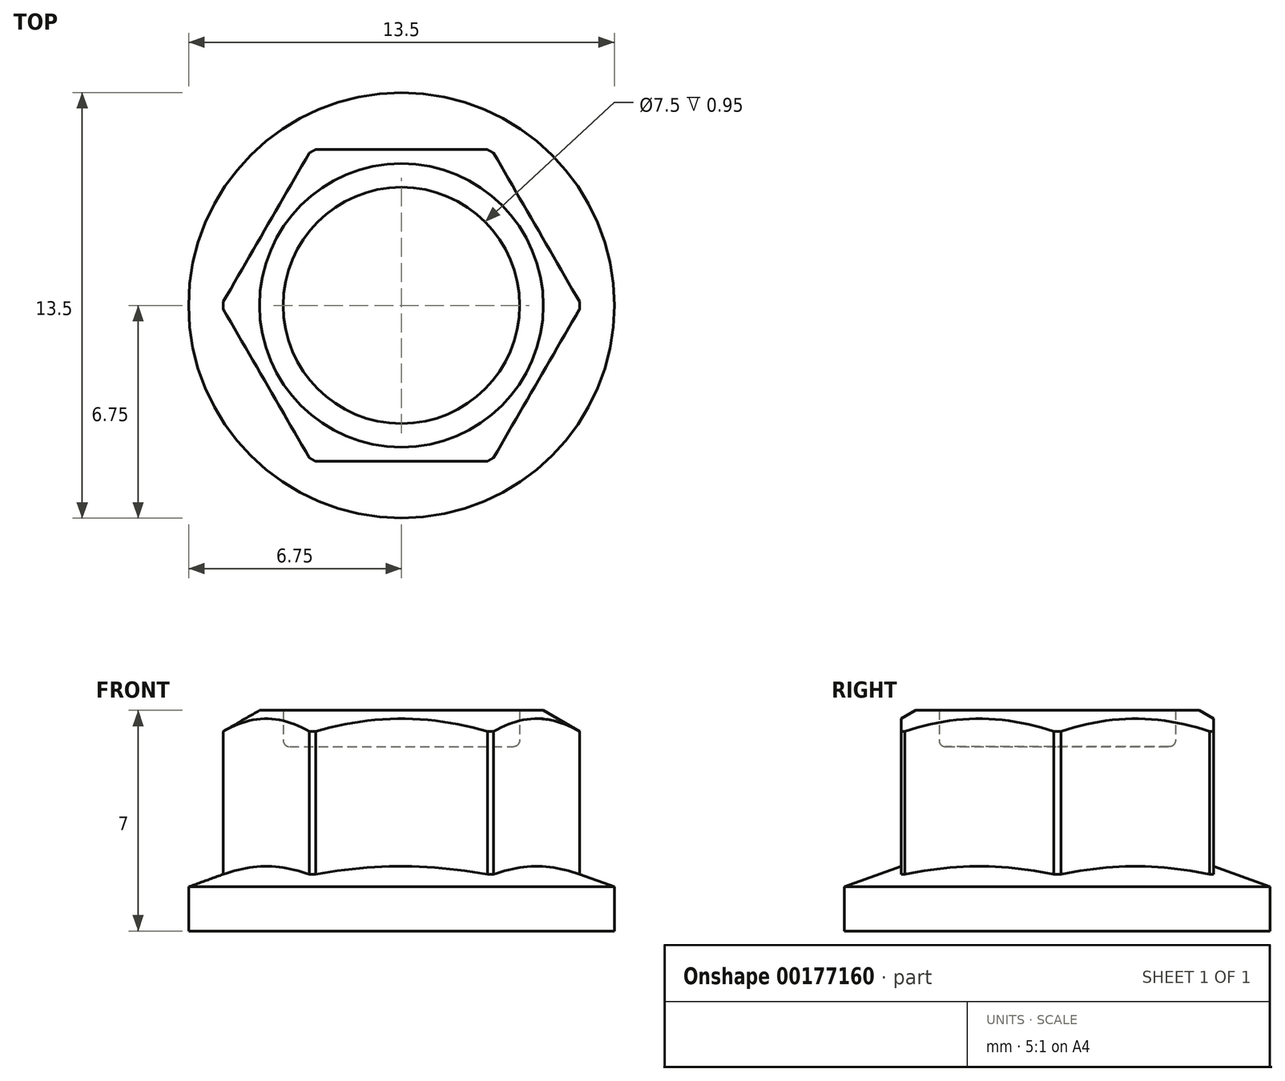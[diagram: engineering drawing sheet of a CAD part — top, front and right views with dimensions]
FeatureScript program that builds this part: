
annotation { "Feature Type Name" : "Feature", "Feature Type Description" : "" }
export const myFeature = defineFeature(function(context is Context, id is Id, definition is map)
    precondition{}
    {
        {
            var Q0;
            Q0=qCreatedBy(makeId("Front.planeOp"),FACE);
            var sketch = newSketch(context, id + "F0", { "sketchPlane" : qUnion([Q0])});
            skLineSegment(sketch, "E0", {"start": v(0, 0) * mm, "end": v(0, 5.85) * mm});
            skLineSegment(sketch, "E1", {"start": v(3.75, 7) * mm, "end": v(4.5, 7) * mm});
            skLineSegment(sketch, "E2", {"start": v(5.65, 6.34) * mm, "end": v(5.65, 1.8) * mm});
            skLineSegment(sketch, "E3", {"start": v(5.65, 1.8) * mm, "end": v(6.75, 1.4) * mm});
            skLineSegment(sketch, "E4", {"start": v(6.75, 1.4) * mm, "end": v(6.75, 0) * mm});
            skLineSegment(sketch, "E5", {"start": v(6.75, 0) * mm, "end": v(0, 0) * mm});
            skLineSegment(sketch, "E6", {"start": v(4.5, 7) * mm, "end": v(5.65, 6.34) * mm});
            skLineSegment(sketch, "E7", {"start": v(3.75, 7) * mm, "end": v(3.75, 6.05) * mm});
            skLineSegment(sketch, "E8", {"start": v(3.55, 5.85) * mm, "end": v(0, 5.85) * mm});
            skPoint(sketch, "E9.visualSharp", {"position": v(3.75, 5.85) * mm});
            skArc(sketch, "E9.filletArc", {"start": v(3.55, 5.85) * mm, "mid": v(3.7, 5.9) * mm, "end": v(3.75, 6.05) * mm});
            skSolve(sketch);
        }
        {
            var Q0;
            Q0 = qSketchRegion(id + "F0", true);
            var Q1;
            Q1=sQuery(id+"F0.wireOp",EDGE,"E0");
            revolve(context, id + "F1", {"entities" : qUnion([Q0]), "axis" : qUnion([Q1]), "revolveType" : RevolveType.FULL});
        }
        {
            var Q0;
            Q0=makeQuery(id+"F1.opRevolve","SWEPT_FACE",FACE,{"disambiguationData":[OSD([sQuery(id+"F0.wireOp",EDGE,"E1")])]});
            var sketch = newSketch(context, id + "F2", { "sketchPlane" : qUnion([Q0])});
            skCircle(sketch, "E10.cCircle", {"center": v(0, 0) * mm, "radius": 4.95 * mm, "construction": true});
            skLineSegment(sketch, "E10.0", {"start": v(-2.86, 4.95) * mm, "end": v(2.86, 4.95) * mm});
            skLineSegment(sketch, "E10.1", {"start": v(2.86, 4.95) * mm, "end": v(5.72, 0) * mm});
            skLineSegment(sketch, "E10.2", {"start": v(5.72, 0) * mm, "end": v(2.86, -4.95) * mm});
            skLineSegment(sketch, "E10.3", {"start": v(2.86, -4.95) * mm, "end": v(-2.86, -4.95) * mm});
            skLineSegment(sketch, "E10.4", {"start": v(-2.86, -4.95) * mm, "end": v(-5.72, 0) * mm});
            skLineSegment(sketch, "E10.5", {"start": v(-5.72, 0) * mm, "end": v(-2.86, 4.95) * mm});
            skPoint(sketch, "E10.0.midPoint", {"position": v(0, 4.95) * mm});
            skCircle(sketch, "E11", {"center": v(0, 0) * mm, "radius": 9.6 * mm});
            skSolve(sketch);
        }
        {
            var Q0;
            Q0 = qSketchRegion(id + "F2", true);
            var Q1;
            Q1=makeQuery(id+"F1.opRevolve","SWEPT_FACE",FACE,{"disambiguationData":[OSD([sQuery(id+"F0.wireOp",EDGE,"E3")])]});
            extrude(context, id + "F3", {"entities" : qUnion([Q0]), "operationType" : NewBodyOperationType.REMOVE, "endBound" : BoundingType.UP_TO_SURFACE, "oppositeDirection" : true, "endBoundEntityFace" : qUnion([Q1]), "depth" : 25 * mm});
        }
    });
